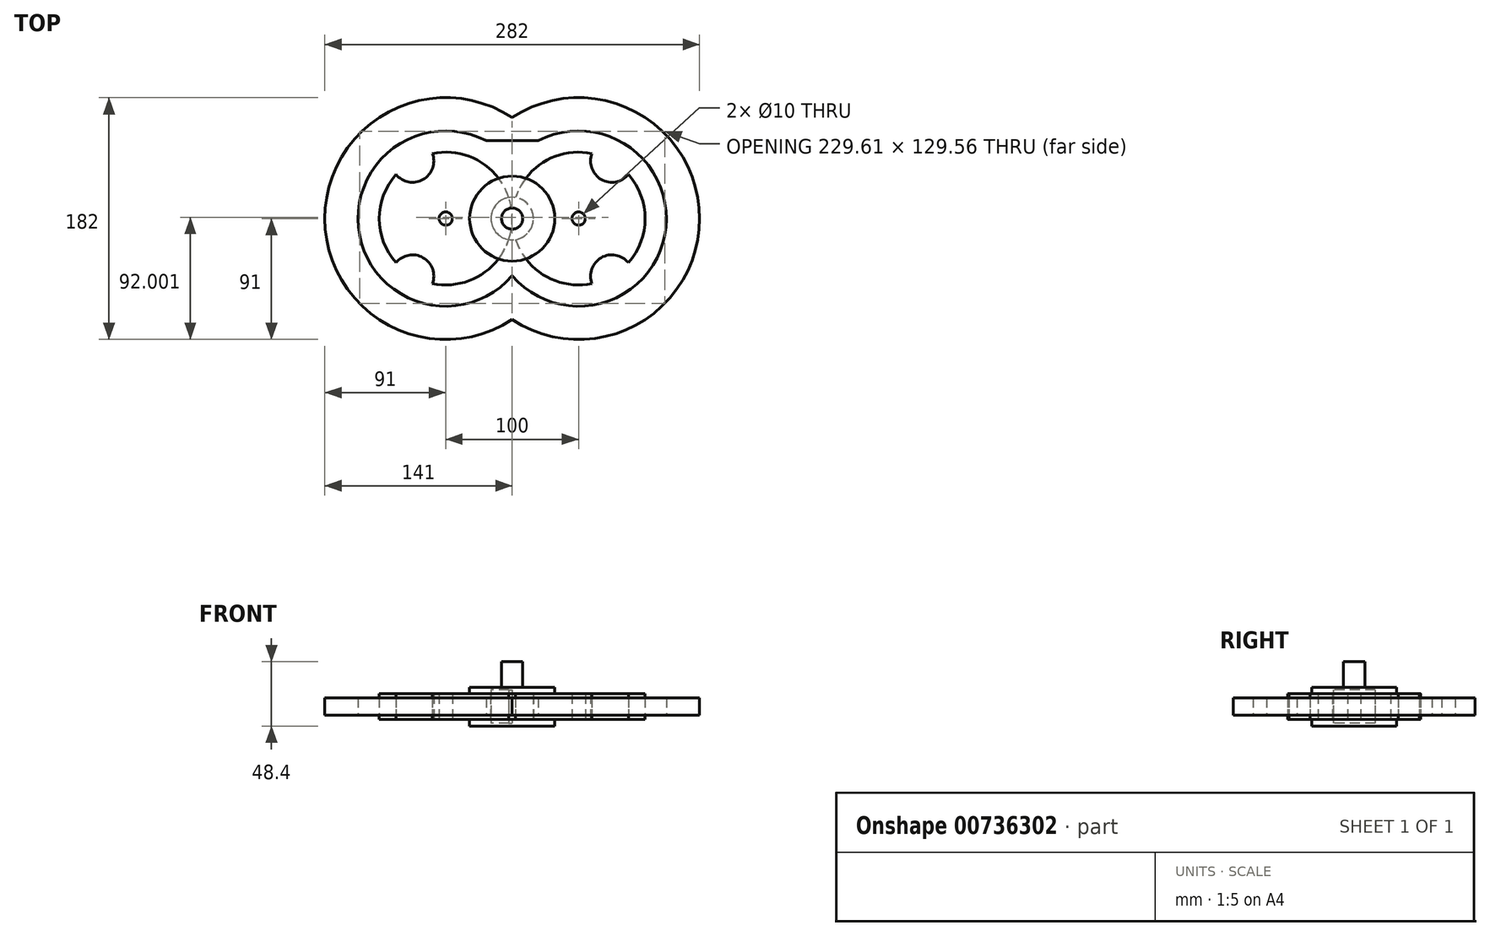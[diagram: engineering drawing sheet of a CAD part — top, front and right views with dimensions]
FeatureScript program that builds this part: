
annotation { "Feature Type Name" : "Feature", "Feature Type Description" : "" }
export const myFeature = defineFeature(function(context is Context, id is Id, definition is map)
    precondition{}
    {
        {
            var Q0;
            Q0=qCreatedBy(makeId("Top.planeOp"),FACE);
            var sketch = newSketch(context, id + "F0", { "sketchPlane" : qUnion([Q0])});
            skLineSegment(sketch, "E0", {"start": v(0, 0) * mm, "end": v(-169.53, 0) * mm, "construction": true});
            skCircle(sketch, "E1", {"center": v(-50, 0) * mm, "radius": 50 * mm});
            skCircle(sketch, "E2", {"center": v(0, 0) * mm, "radius": 16 * mm});
            skLineSegment(sketch, "E3", {"start": v(-50, 0) * mm, "end": v(-75, 43.3) * mm, "construction": true});
            skLineSegment(sketch, "E4", {"start": v(-50, 0) * mm, "end": v(-75, -43.3) * mm, "construction": true});
            skCircle(sketch, "E5", {"center": v(-75, 43.3) * mm, "radius": 16 * mm});
            skCircle(sketch, "E6", {"center": v(-75, -43.3) * mm, "radius": 16 * mm});
            skCircle(sketch, "E7", {"center": v(-50, 0) * mm, "radius": 5 * mm});
            skSolve(sketch);
        }
        {
            var Q0;
            {var subQ1=sQuery(id+"F0.wireOp",EDGE,"E1");var subQ6=sQuery(id+"F0.wireOp",EDGE,"E5");var subQ9=makeQuery(id+"F0.imprint","INTERSECT",VERTEX,{"disambiguationData":[OD(0.0)],"derivedFrom":[subQ1,subQ6]});Q0=makeQuery(id+"F0.imprint","IMPRINT",FACE,{"disambiguationData":[TD([[makeQuery(id+"F0.imprint","IMPRINT",EDGE,{"disambiguationData":[TD([[subQ9,1.0]])],"derivedFrom":subQ1}),1.0]])]});}
            extrude(context, id + "F1", {"entities" : qUnion([Q0]), "endBound" : BoundingType.SYMMETRIC, "depth" : 19.2 * mm, "offsetDistance" : 25 * mm});
        }
        {
            var Q0;
            {var subQ0=sQuery(id+"F0.wireOp",EDGE,"E2");var subQ1=sQuery(id+"F0.wireOp",EDGE,"E1");var subQ2=makeQuery(id+"F0.imprint","INTERSECT",VERTEX,{"disambiguationData":[OD(0.0)],"derivedFrom":[subQ1,subQ0]});Q0=makeQuery(id+"F0.imprint","IMPRINT",FACE,{"disambiguationData":[TD([[makeQuery(id+"F0.imprint","IMPRINT",EDGE,{"disambiguationData":[TD([[subQ2,1.0]])],"derivedFrom":subQ1}),1.0]])]});}
            extrude(context, id + "F2", {"entities" : qUnion([Q0]), "endBound" : BoundingType.SYMMETRIC, "depth" : 25 * mm, "offsetDistance" : 25 * mm});
        }
        {
            var Q0;
            Q0=qCreatedBy(makeId("Front.planeOp"),FACE);
            var sketch = newSketch(context, id + "F3", { "sketchPlane" : qUnion([Q0])});
            skLineSegment(sketch, "E8", {"start": v(0, 12.5) * mm, "end": v(0, -12.5) * mm});
            skLineSegment(sketch, "E9", {"start": v(-16, -9.6) * mm, "end": v(-16, 9.6) * mm});
            skLineSegment(sketch, "E10", {"start": v(-16, 9.6) * mm, "end": v(0, 9.6) * mm});
            skLineSegment(sketch, "E11", {"start": v(-16, -9.6) * mm, "end": v(0, -9.6) * mm});
            skLineSegment(sketch, "E12", {"start": v(-16, 9.6) * mm, "end": v(-32, 9.6) * mm});
            skLineSegment(sketch, "E13", {"start": v(-32, 9.6) * mm, "end": v(-32, 14.6) * mm});
            skLineSegment(sketch, "E14", {"start": v(-32, 14.6) * mm, "end": v(0, 14.6) * mm});
            skLineSegment(sketch, "E15", {"start": v(-16, -9.6) * mm, "end": v(-32, -9.6) * mm});
            skLineSegment(sketch, "E16", {"start": v(-32, -9.6) * mm, "end": v(-32, -14.6) * mm});
            skLineSegment(sketch, "E17", {"start": v(-32, -14.6) * mm, "end": v(0, -14.6) * mm});
            skLineSegment(sketch, "E18", {"start": v(0, 12.5) * mm, "end": v(0, 33.8) * mm});
            skLineSegment(sketch, "E19", {"start": v(0, 33.8) * mm, "end": v(-8, 33.8) * mm});
            skLineSegment(sketch, "E20", {"start": v(-8, 33.8) * mm, "end": v(-8, 14.6) * mm});
            skLineSegment(sketch, "E21", {"start": v(0, -12.5) * mm, "end": v(0, -14.6) * mm});
            skSolve(sketch);
        }
        {
            var Q0;
            {var subQ0=sQuery(id+"F3.wireOp",EDGE,"E18");Q0=makeQuery(id+"F3.imprint","IMPRINT",FACE,{"disambiguationData":[TD([[makeQuery(id+"F3.imprint","IMPRINT",EDGE,{"derivedFrom":subQ0}),1.0]])]});}
            var Q1;
            {var subQ1=sQuery(id+"F3.wireOp",EDGE,"E10");Q1=makeQuery(id+"F3.imprint","IMPRINT",FACE,{"disambiguationData":[TD([[makeQuery(id+"F3.imprint","IMPRINT",EDGE,{"derivedFrom":subQ1}),1.0]])]});}
            var Q2;
            Q2=makeQuery(id+"F3.imprint","IMPRINT",FACE,{"disambiguationData":[TD([[makeQuery(id+"F3.imprint","IMPRINT",EDGE,{"derivedFrom":sQuery(id+"F3.wireOp",EDGE,"E9")}),-1.0]])]});
            var Q3;
            {var subQ0=sQuery(id+"F3.wireOp",EDGE,"E11");Q3=makeQuery(id+"F3.imprint","IMPRINT",FACE,{"disambiguationData":[TD([[makeQuery(id+"F3.imprint","IMPRINT",EDGE,{"derivedFrom":subQ0}),-1.0]])]});}
            var Q4;
            {var subQ0=sQuery(id+"F3.wireOp",EDGE,"32C2RPK8-S2aX-Ap7T-tmnl-ecLvW3LFVPhI");Q4=makeQuery(id+"F3.imprint","IMPRINT",FACE,{"disambiguationData":[TD([[makeQuery(id+"F3.imprint","IMPRINT",EDGE,{"derivedFrom":subQ0}),1.0]])]});}
            var Q5;
            Q5=sQuery(id+"F3.wireOp",EDGE,"E8");
            revolve(context, id + "F4", {"surfaceOperationType" : NewSurfaceOperationType.NEW, "entities" : qUnion([Q0, Q1, Q2, Q3, Q4]), "axis" : qUnion([Q5]), "revolveType" : RevolveType.FULL});
        }
        {
            var Q0;
            Q0=makeQuery(id+"F1.opExtrude","SWEPT_BODY",BODY,{"disambiguationData":[OSD([sQuery(id+"F0.wireOp",EDGE,"E1"),sQuery(id+"F0.wireOp",EDGE,"E2"),sQuery(id+"F0.wireOp",EDGE,"E5"),sQuery(id+"F0.wireOp",EDGE,"E6"),sQuery(id+"F0.wireOp",EDGE,"E7")])]});
            var Q1;
            Q1=qCreatedBy(makeId("Right.planeOp"),FACE);
            mirror(context, id + "F5", {"entities" : qUnion([Q0]), "mirrorPlane" : qUnion([Q1])});
        }
        {
            var Q0;
            Q0=qCreatedBy(makeId("Top.planeOp"),FACE);
            var sketch = newSketch(context, id + "F6", { "sketchPlane" : qUnion([Q0])});
            skCircle(sketch, "E22.0", {"center": v(-50, 0) * mm, "radius": 5 * mm, "construction": true});
            skCircle(sketch, "E23.0", {"center": v(0, 0) * mm, "radius": 16 * mm, "construction": true});
            skCircle(sketch, "E24.0", {"center": v(50, 0) * mm, "radius": 5 * mm, "construction": true});
            skLineSegment(sketch, "E25", {"start": v(41, 0) * mm, "end": v(16, 0) * mm, "construction": true});
            skLineSegment(sketch, "E26", {"start": v(-16, 0) * mm, "end": v(-41, 0) * mm, "construction": true});
            skArc(sketch, "E27", {"start": v(0, 76.03) * mm, "mid": v(-41, 0) * mm, "end": v(0, -76.03) * mm, "construction": true});
            skArc(sketch, "E28", {"start": v(0, -76.03) * mm, "mid": v(141, 0) * mm, "end": v(0, 76.03) * mm});
            skArc(sketch, "E29", {"start": v(0, 76.03) * mm, "mid": v(-141, 0) * mm, "end": v(0, -76.03) * mm});
            skArc(sketch, "E30", {"start": v(0, -76.03) * mm, "mid": v(10.44, -68.03) * mm, "end": v(19.63, -58.6) * mm, "construction": true});
            skLineSegment(sketch, "E31", {"start": v(-19.62, 58.6) * mm, "end": v(19.63, 58.6) * mm});
            skArc(sketch, "E32", {"start": v(-19.63, 58.6) * mm, "mid": v(-116, 0) * mm, "end": v(-19.62, -58.6) * mm});
            skLineSegment(sketch, "E33", {"start": v(-19.62, -58.6) * mm, "end": v(-19.62, -58.6) * mm});
            skArc(sketch, "E34", {"start": v(19.62, 58.6) * mm, "mid": v(-14.8, 12.5) * mm, "end": v(0, -43.08) * mm, "construction": true});
            skArc(sketch, "E35", {"start": v(19.62, -58.6) * mm, "mid": v(19.83, -58.7) * mm, "end": v(20.03, -58.8) * mm});
            skArc(sketch, "E36", {"start": v(0, -43.08) * mm, "mid": v(14.8, 12.5) * mm, "end": v(-19.62, 58.6) * mm, "construction": true});
            skArc(sketch, "E37", {"start": v(-19.62, -58.6) * mm, "mid": v(-9.07, -51.78) * mm, "end": v(0, -43.08) * mm});
            skLineSegment(sketch, "E38", {"start": v(0, -43.08) * mm, "end": v(0, -43.08) * mm});
            skArc(sketch, "E39", {"start": v(20.03, -58.8) * mm, "mid": v(116, 0.23) * mm, "end": v(19.63, 58.6) * mm});
            skArc(sketch, "E40", {"start": v(0, -43.08) * mm, "mid": v(9.07, -51.78) * mm, "end": v(19.62, -58.6) * mm});
            skArc(sketch, "E41", {"start": v(19.62, -58.6) * mm, "mid": v(40.05, 13.13) * mm, "end": v(0, 76.03) * mm, "construction": true});
            skSolve(sketch);
        }
        {
            var Q0;
            Q0=makeQuery(id+"F6.imprint","IMPRINT",FACE,{"disambiguationData":[TD([[makeQuery(id+"F6.imprint","IMPRINT",EDGE,{"derivedFrom":sQuery(id+"F6.wireOp",EDGE,"E28")}),1.0]])]});
            var Q1;
            Q1=makeQuery(id+"F4.opRevolve","SWEPT_FACE",FACE,{"disambiguationData":[OSD([sQuery(id+"F3.wireOp",EDGE,"E12")])]});
            var Q2;
            Q2=makeQuery(id+"F4.opRevolve","SWEPT_FACE",FACE,{"disambiguationData":[OSD([sQuery(id+"F3.wireOp",EDGE,"E15")])]});
            extrude(context, id + "F7", {"entities" : qUnion([Q0]), "endBound" : BoundingType.UP_TO_SURFACE, "depth" : 25 * mm, "endBoundEntityFace" : qUnion([Q1]), "hasOffset" : true, "offsetDistance" : 3 * mm, "hasSecondDirection" : true, "secondDirectionBound" : SecondDirectionBoundingType.UP_TO_SURFACE, "secondDirectionOppositeDirection" : true, "secondDirectionDepth" : 25 * mm, "secondDirectionBoundEntityFace" : qUnion([Q2]), "hasSecondDirectionOffset" : true, "secondDirectionOffsetDistance" : 3 * mm});
        }
    });
